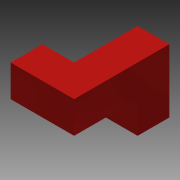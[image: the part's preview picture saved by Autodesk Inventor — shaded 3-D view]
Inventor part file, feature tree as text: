
AUTODESK INVENTOR PART (.ipt)
format: ipt  version: 2015 (Build 190159000, 159)  size: 110,592 bytes
history: native  units: in
note: dims shown in document units (in); Inventor stores cm internally (conversion verified against a paired STEP export)
features: extrude x3, sketch x3
ambient origin geometry x8: Origin, YZ Plane, XZ Plane, XY Plane, X Axis, Y Axis, Z Axis, Center Point
bodies: Solid1 (feature_tree)
feature tree (6):
  extrude  "Extrusion1"  Depth=0.75in
  extrude  "Extrusion2"  Depth=0.75in
  extrude  "Extrusion3"  Depth=0.75in TaperAngle=0.0deg
  sketch  "Sketch1"  dims[d0=1.5in d1=0.75in]
  sketch  "Sketch2"  dims[d2=2.25in d3=0.75in]
  sketch  "Sketch3"  dims[d4=1.5in d5=0.75in d6=0.0in d7=0.75in d8=0.0in d9=0.75in d10=0.75in d11=0.0in]
